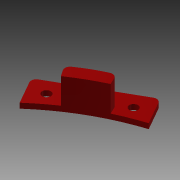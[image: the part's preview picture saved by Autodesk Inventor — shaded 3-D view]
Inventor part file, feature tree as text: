
AUTODESK INVENTOR PART (.ipt)
format: ipt  version: 2015 SP1 (Build 190203100, 203)  size: 116,224 bytes
history: native  units: mm
features: reference x5, extrude x2, sketch x2, plane x1
ambient origin geometry x8: Origin, YZ Plane, XZ Plane, XY Plane, X Axis, Y Axis, Z Axis, Center Point
bodies: Solid1 (feature_tree)
feature tree (10):
  plane  "Work Plane1"
  extrude  "Extrusion1"  Depth=12.0mm
  extrude  "Extrusion2"  Depth=10.0mm
  sketch  "Sketch1"  dims[d0=12.0mm d1=12.0mm]
  reference  "Reference1"
  reference  "Reference2"
  reference  "Reference5"
  reference  "Reference6"
  reference  "Reference7"
  sketch  "Sketch2"  dims[d2=2.0mm d4=180.0mm d5=2.0mm d6=0.0mm d7=10.0mm d8=10.0mm d9=2.0mm d10=10.0mm d11=0.0mm]
